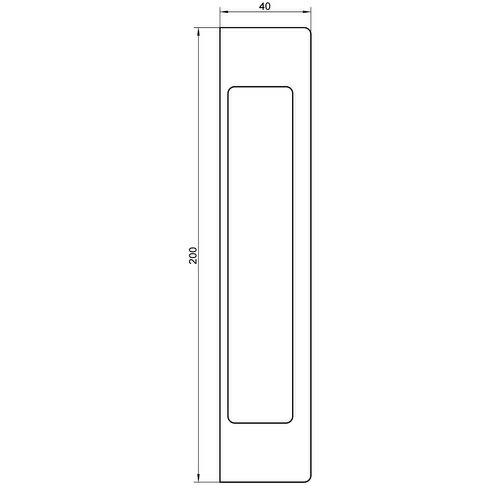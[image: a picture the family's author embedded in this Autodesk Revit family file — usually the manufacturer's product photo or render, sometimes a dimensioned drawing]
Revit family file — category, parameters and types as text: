
# Revit family: Prime
name_source: partatom
category: Furniture Systems
revit_build: Autodesk Revit 2017 (Build: 20190508_0315(x64)
units: mm (PartAtom-declared; Revit-internal decimal feet)

## family parameters
Always vertical = Yes
Cut with Voids When Loaded = No
OmniClass Number = 23.40.70.14.64.21.14
OmniClass Title = Free-Standing Component
Part Type = Normal
Room Calculation Point = No
Round Connector Dimension = Use Diameter
Shared = No
Work Plane-Based = No

## types (1)
- default
    Carpet Material = SilentLab - Carpet
    Fitting Material = SilentLab - Fitting - Brushed stainles steel RAL 9016
    Frame Material = SilentLab - Frame - Oak standard
    Glass Material = SilentLab - Glass
    Handle Default = Yes
    Handle Material = SilentLab - Handle - Brushed stainles steel
    Handle Tectus = No
    Height = 2270 mm  [stored 7.44751 ft]
    Leg Height = 40 mm  [stored 0.131234 ft]
    Length = 1000 mm  [stored 3.28084 ft]
    Light on = Yes
    Material = SilentLab - Fabric - Medley_66145
    Panel Height = 339 mm  [stored 1.1122 ft]
    Table Material = SilentLab - Handle - Oak standard
    Width = 1150 mm

note: [stored X ft] marks values corroborated as IEEE doubles in the binary element streams (Revit-internal decimal feet)

## geometry (parser evidence)
native form markers: Sweep x10
no freeform markers — native parametric forms only
